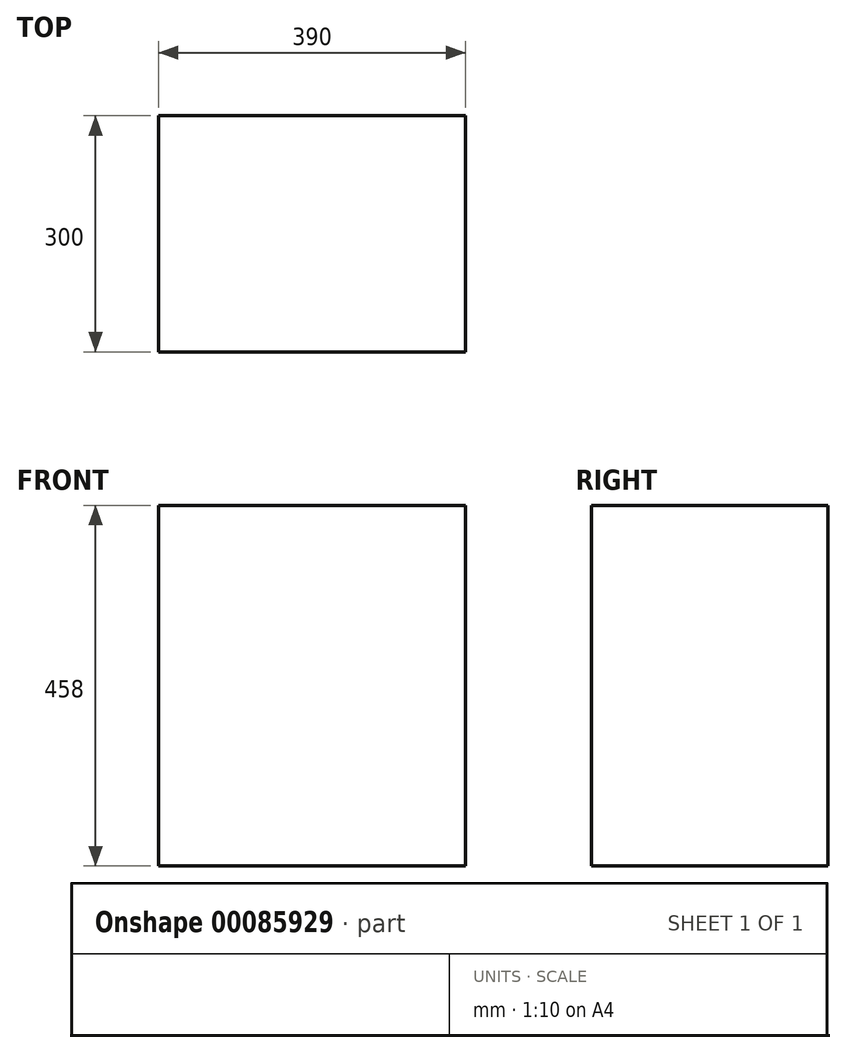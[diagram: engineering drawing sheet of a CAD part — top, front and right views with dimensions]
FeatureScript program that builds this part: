
annotation { "Feature Type Name" : "Feature", "Feature Type Description" : "" }
export const myFeature = defineFeature(function(context is Context, id is Id, definition is map)
    precondition{}
    {
        {
            var Q0;
            Q0=qCreatedBy(makeId("Top.planeOp"),FACE);
            var sketch = newSketch(context, id + "F0", { "sketchPlane" : qUnion([Q0])});
            skLineSegment(sketch, "E0", {"start": v(0, 0) * mm, "end": v(390, 0) * mm});
            skLineSegment(sketch, "E1", {"start": v(390, 0) * mm, "end": v(390, 300) * mm});
            skLineSegment(sketch, "E2", {"start": v(390, 300) * mm, "end": v(0, 300) * mm});
            skLineSegment(sketch, "E3", {"start": v(0, 300) * mm, "end": v(0, 0) * mm});
            skSolve(sketch);
        }
        {
            var Q0;
            Q0=makeQuery(id+"F0.imprint","IMPRINT",FACE,{"disambiguationData":[TD([[makeQuery(id+"F0.imprint","IMPRINT",EDGE,{"derivedFrom":sQuery(id+"F0.wireOp",EDGE,"E0")}),1.0]])]});
            extrude(context, id + "F1", {"entities" : qUnion([Q0]), "depth" : 458 * mm});
        }
    });
